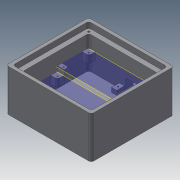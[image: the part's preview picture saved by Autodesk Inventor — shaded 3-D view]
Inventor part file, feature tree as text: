
AUTODESK INVENTOR PART (.ipt)
format: ipt  version: 2014 SP1 (Build 180222100, 222)  size: 397,312 bytes
history: native  units: in
note: dims shown in document units (in); Inventor stores cm internally (conversion verified against a paired STEP export)
features: extrude x12, sketch x12, projected_geometry x5, reference x3, fillet x2, plane x2
ambient origin geometry x8: Origin, YZ Plane, XZ Plane, XY Plane, X Axis, Y Axis, Z Axis, Center Point
bodies: Solid1 (feature_tree)
feature tree (36):
  extrude  "Extrusion1"  Depth=3.25in
  extrude  "Extrusion2"  Depth=0.1969in TaperAngle=0.0deg
  fillet  "Fillet1"  Radius=3.375in
  extrude  "Extrusion3"  Depth=0.3937in
  extrude  "Extrusion4"  Depth=1.5748in TaperAngle=0.0deg
  plane  "Work Plane1"
  extrude  "Extrusion6"  Depth=0.1875in
  fillet  "Fillet2"  Radius=0.1875in
  extrude  "Extrusion7"  Depth=0.375in
  extrude  "Extrusion8"  Depth=0.125in
  extrude  "Extrusion9"  Depth=0.1875in
  plane  "Work Plane2"
  extrude  "Extrusion10"  Depth=0.375in
  extrude  "Extrusion11"  Depth=0.75in
  extrude  "Extrusion12"  Depth=0.3937in
  extrude  "Extrusion13"  Depth=0.2362in
  sketch  "Sketch1"  dims[d0=3.375in d1=3.25in]
  sketch  "Sketch2"  dims[d2=0.3937in d3=0.1969in d4=0.0in d5=3.375in]
  sketch  "Sketch3"  dims[d6=3.25in d7=0.3937in]
  sketch  "Sketch4"  dims[d8=0.3937in d9=1.5748in d10=0.0in]
  sketch  "Sketch6"  dims[d11=0.125in d12=0.1875in d13=0.1875in]
  sketch  "Sketch7"  dims[d14=0.1875in d15=0.375in]
  sketch  "Sketch8"  dims[d16=0.375in d17=0.125in]
  reference  "Reference5"
  projected_geometry  "Projected Loop2"
  sketch  "Sketch9"  dims[d18=0.1875in d19=0.1875in]
  projected_geometry  "Projected Loop3"
  projected_geometry  "Projected Loop4"
  sketch  "Sketch10"  dims[d20=0.375in d21=0.375in]
  projected_geometry  "Projected Loop5"
  sketch  "Sketch11"  dims[d22=0.75in d23=0.75in]
  reference  "Reference7"
  reference  "Reference8"
  sketch  "Sketch12"  dims[d24=0.3937in d25=0.0in d26=0.481in]
  sketch  "Sketch13"  dims[d27=0.7559in d28=0.25in d29=0.375in d30=0.0in d31=0.25in d36=0.2756in d37=0.0in d38=0.1575in d39=0.1575in d40=0.1575in d41=0.1575in d42=0.125in d44=0.2756in d45=0.1in d46=0.5in d47=0.0in d49=0.06in d50=0.375in d51=0.0in d52=0.06in d53=0.06in d54=0.06in d55=0.5in d56=0.0in d57=0.2362in d58=0.2362in d59=0.2362in d60=0.2362in d61=0.375in d62=0.0in d63=0.06in d64=0.06in d65=0.06in d66=0.06in d67=0.06in d68=0.06in d69=0.315in d70=0.0in d71=0.2756in d72=0.1378in d73=0.2165in d74=0.1181in d75=0.0787in d76=0.0in d77=0.1181in d78=0.0591in d79=0.2362in d80=0.0in]
  projected_geometry  "Projected Loop6"
